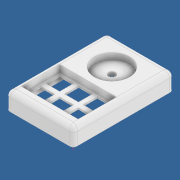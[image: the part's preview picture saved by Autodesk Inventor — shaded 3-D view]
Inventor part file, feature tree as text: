
AUTODESK INVENTOR PART (.ipt)
format: ipt  version: 2020 (Build 240168000, 168)  size: 442,880 bytes
history: native  units: in
note: dims shown in document units (in); Inventor stores cm internally (conversion verified against a paired STEP export)
features: sketch x12, extrude x11, fillet x3, chamfer x1
ambient origin geometry x8: Origin, YZ Plane, XZ Plane, XY Plane, X Axis, Y Axis, Z Axis, Center Point
bodies: Solid1 (feature_tree)
feature tree (27):
  extrude  "Extrusion1"  Depth=2.6299in
  extrude  "Extrusion2"  Depth=1.4961in
  extrude  "Extrusion3"  Depth=0.3937in
  extrude  "Extrusion4"  Depth=0.5433in
  extrude  "Extrusion5"  Depth=0.5433in
  extrude  "Extrusion6"  Depth=0.5433in
  extrude  "Extrusion7"  Depth=0.5433in
  fillet  "Fillet4"  Radius=0.5512in
  extrude  "Extrusion9"  Depth=0.0591in TaperAngle=0.0deg
  extrude  "Extrusion10"  Depth=0.2598in TaperAngle=0.0deg
  extrude  "Extrusion11"  Depth=1.315in
  fillet  "Fillet5"  Radius=0.2677in
  extrude  "Extrusion12"  Depth=1.1083in
  sketch  "Sketch16"  dims[d44=0.1575in d45=0.1575in d46=0.3819in d47=0.0in d48=0.1575in d49=0.1575in d50=2.5118in d51=3.7795in d52=0.0787in d53=0.0591in d54=0.0709in d55=0.0in d63=0.0591in d64=0.1929in d65=0.185in d66=0.185in d67=0.1929in d69=0.2028in d70=0.311in d71=0.0in d72=0.1339in d73=0.1339in d74=0.1339in d75=0.1339in d76=0.0551in d77=0.0551in d78=0.0551in d79=0.0551in d80=0.1063in d81=0.1063in d82=0.1063in d83=0.1063in d84=0.1063in d85=0.1063in d86=0.1063in d87=0.1063in d88=0.2165in d89=0.0in d90=0.7874in d91=0.0787in d92=0.0in d101=0.1575in d110=0.1122in d111=0.1083in d112=0.1181in d113=0.0787in d114=0.1969in d115=0.0591in d116=0.0787in d117=0.0in d118=0.2028in d134=0.0197in d135=0.0787in d136=45.0deg d56=0.0197in d57=0.0344in d58=0.0197in d59=0.0344in d137=0.0344in]
  fillet  "Fillet6"  Radius=0.3307in
  chamfer  "Chamfer3"  Distance=0.1575in
  sketch  "Sketch1"  dims[d0=2.6299in d1=3.937in]
  sketch  "Sketch2"  dims[d2=0.7087in d3=0.0in d6=1.4961in]
  sketch  "Sketch3"  dims[d7=0.2028in d8=0.3937in]
  sketch  "Sketch4"  dims[d9=0.2677in d10=0.0in d12=0.5433in]
  sketch  "Sketch7"  dims[d13=0.5433in d14=0.5433in]
  sketch  "Sketch8"  dims[d15=0.5433in d16=0.5433in]
  sketch  "Sketch10"  dims[d17=0.5512in d18=0.5433in d19=0.5512in]
  sketch  "Sketch12"  dims[d26=0.5512in d27=0.0591in d28=0.0in]
  sketch  "Sketch13"  dims[d30=1.378in d33=0.2598in d34=0.0in]
  sketch  "Sketch14"  dims[d35=2.8287in d36=1.315in d37=0.2677in]
  sketch  "Sketch15"  dims[d38=1.315in d39=1.1083in d40=0.3307in d41=0.0in]
